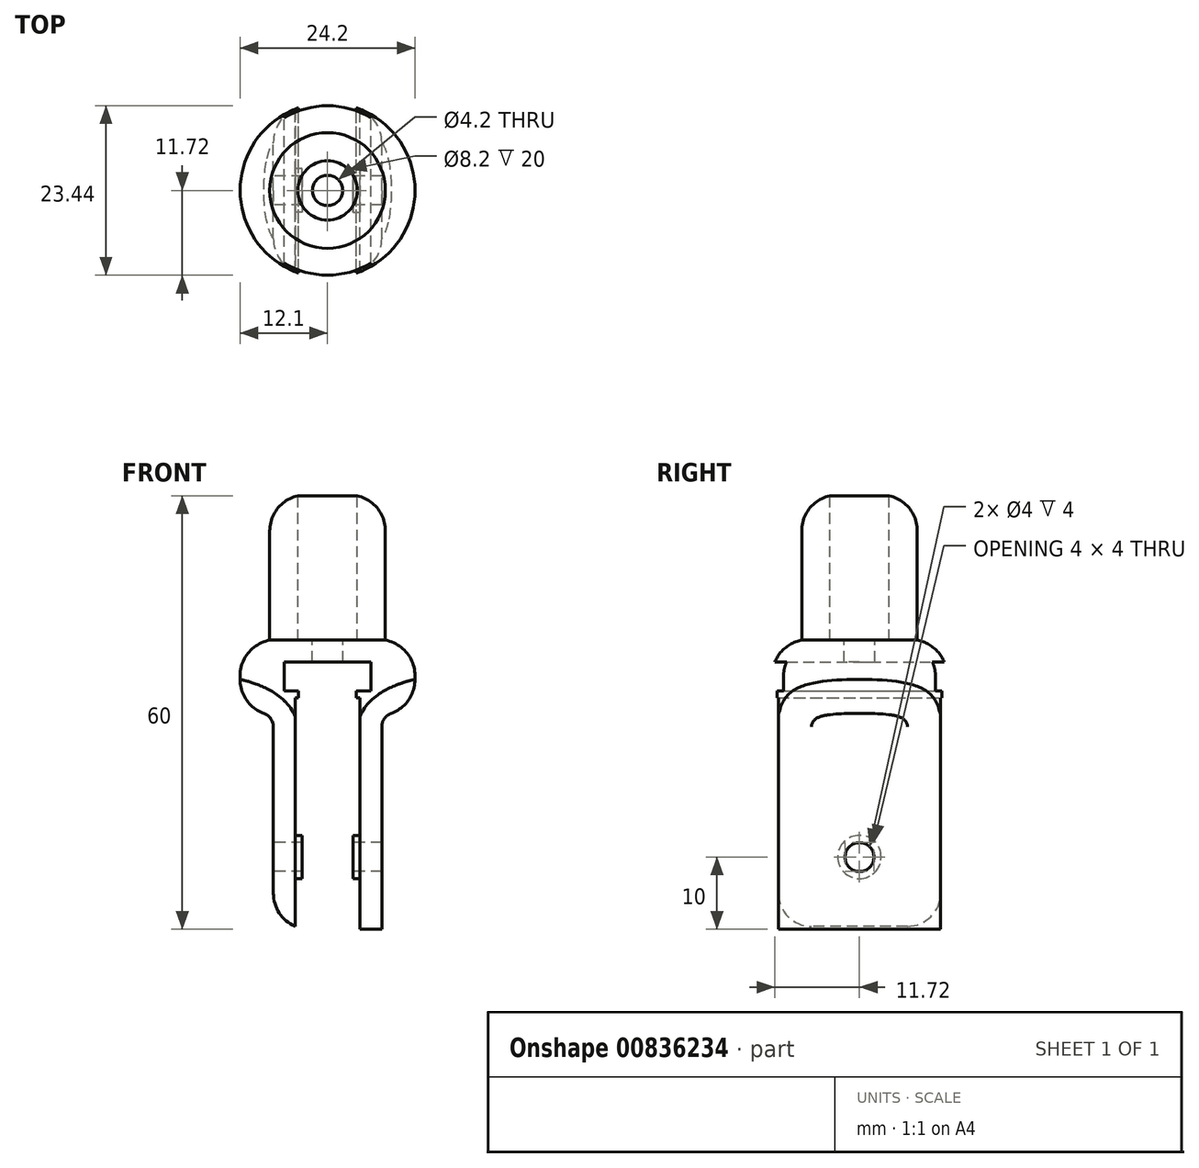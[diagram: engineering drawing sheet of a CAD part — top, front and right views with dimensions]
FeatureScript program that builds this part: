
annotation { "Feature Type Name" : "Feature", "Feature Type Description" : "" }
export const myFeature = defineFeature(function(context is Context, id is Id, definition is map)
    precondition{}
    {
        {
            var Q0;
            Q0=qCreatedBy(makeId("Front.planeOp"),FACE);
            var sketch = newSketch(context, id + "F0", { "sketchPlane" : qUnion([Q0])});
            skLineSegment(sketch, "E0.bottom", {"start": v(-8, 20) * mm, "end": v(-4.1, 20) * mm});
            skLineSegment(sketch, "E0.top", {"start": v(-8, 0) * mm, "end": v(-4.1, 0) * mm});
            skLineSegment(sketch, "E0.left", {"start": v(-8, 20) * mm, "end": v(-8, 0) * mm});
            skLineSegment(sketch, "E0.right", {"start": v(-4.1, 20) * mm, "end": v(-4.1, 0) * mm});
            skLineSegment(sketch, "E1.bottom", {"start": v(-12.1, 0) * mm, "end": v(-2.1, 0) * mm});
            skLineSegment(sketch, "E1.top", {"start": v(-12.1, -40) * mm, "end": v(-2.1, -40) * mm});
            skLineSegment(sketch, "E1.left", {"start": v(-12.1, 0) * mm, "end": v(-12.1, -40) * mm});
            skLineSegment(sketch, "E1.right", {"start": v(-2.1, 0) * mm, "end": v(-2.1, -40) * mm});
            skLineSegment(sketch, "E2", {"start": v(0, 18.35) * mm, "end": v(0, -37.68) * mm, "construction": true});
            skSolve(sketch);
        }
        {
            var Q0;
            Q0 = qSketchRegion(id + "F0", true);
            var Q1;
            Q1=sQuery(id+"F0.wireOp",EDGE,"E2");
            revolve(context, id + "F1", {"surfaceOperationType" : NewSurfaceOperationType.NEW, "entities" : qUnion([Q0]), "axis" : qUnion([Q1]), "revolveType" : RevolveType.FULL});
        }
        {
            var Q0;
            Q0=qCreatedBy(makeId("Front.planeOp"),FACE);
            var sketch = newSketch(context, id + "F2", { "sketchPlane" : qUnion([Q0])});
            skLineSegment(sketch, "E3.bottom", {"start": v(4.5, -40) * mm, "end": v(-4.5, -40) * mm});
            skLineSegment(sketch, "E3.top", {"start": v(4.5, -8) * mm, "end": v(-4.5, -8) * mm});
            skLineSegment(sketch, "E3.left", {"start": v(4.5, -40) * mm, "end": v(4.5, -8) * mm});
            skLineSegment(sketch, "E3.right", {"start": v(-4.5, -40) * mm, "end": v(-4.5, -8) * mm});
            skLineSegment(sketch, "E4.bottom", {"start": v(4, -7) * mm, "end": v(-4, -7) * mm});
            skLineSegment(sketch, "E4.top", {"start": v(4, -8) * mm, "end": v(-4, -8) * mm});
            skLineSegment(sketch, "E4.left", {"start": v(4, -7) * mm, "end": v(4, -8) * mm});
            skLineSegment(sketch, "E4.right", {"start": v(-4, -7) * mm, "end": v(-4, -8) * mm});
            skLineSegment(sketch, "E5.bottom", {"start": v(6, -3) * mm, "end": v(-6, -3) * mm});
            skLineSegment(sketch, "E5.top", {"start": v(6, -7) * mm, "end": v(-6, -7) * mm});
            skLineSegment(sketch, "E5.left", {"start": v(6, -3) * mm, "end": v(6, -7) * mm});
            skLineSegment(sketch, "E5.right", {"start": v(-6, -3) * mm, "end": v(-6, -7) * mm});
            skLineSegment(sketch, "E6.bottom", {"start": v(-9.5, -10) * mm, "end": v(-12.1, -10) * mm});
            skLineSegment(sketch, "E6.top", {"start": v(-7.5, -40) * mm, "end": v(-12.1, -40) * mm});
            skLineSegment(sketch, "E6.left", {"start": v(-7.5, -12) * mm, "end": v(-7.5, -40) * mm});
            skLineSegment(sketch, "E6.right", {"start": v(-12.1, -10) * mm, "end": v(-12.1, -40) * mm});
            skPoint(sketch, "E7.visualSharp", {"position": v(-7.5, -10) * mm});
            skArc(sketch, "E7.filletArc", {"start": v(-7.5, -12) * mm, "mid": v(-8.09, -10.59) * mm, "end": v(-9.5, -10) * mm});
            skLineSegment(sketch, "E8.MirrorCS", {"start": v(7.5, -12) * mm, "end": v(7.5, -40) * mm});
            skArc(sketch, "E9.MirrorCS", {"start": v(7.5, -12) * mm, "mid": v(8.09, -10.59) * mm, "end": v(9.5, -10) * mm});
            skLineSegment(sketch, "E10.MirrorCS", {"start": v(9.5, -10) * mm, "end": v(12.1, -10) * mm});
            skLineSegment(sketch, "E11.MirrorCS", {"start": v(12.1, -10) * mm, "end": v(12.1, -40) * mm});
            skLineSegment(sketch, "E12.MirrorCS", {"start": v(7.5, -40) * mm, "end": v(12.1, -40) * mm});
            skSolve(sketch);
        }
        {
            var Q0;
            Q0 = qSketchRegion(id + "F2", true);
            extrude(context, id + "F3", {"entities" : qUnion([Q0]), "operationType" : NewBodyOperationType.REMOVE, "endBound" : BoundingType.SYMMETRIC, "depth" : 50 * mm, "offsetDistance" : 25 * mm});
        }
        {
            var Q0;
            Q0=makeQuery(id+"F3.boolean.opBoolean","COPY",FACE,{"derivedFrom":makeQuery(id+"F3.opExtrude","SWEPT_FACE",FACE,{"disambiguationData":[OSD([sQuery(id+"F2.wireOp",EDGE,"E3.left")])]})});
            var sketch = newSketch(context, id + "F4", { "sketchPlane" : qUnion([Q0])});
            skCircle(sketch, "E13", {"center": v(0, -30) * mm, "radius": 2 * mm});
            skSolve(sketch);
        }
        {
            var Q0;
            Q0 = qSketchRegion(id + "F4", true);
            extrude(context, id + "F5", {"entities" : qUnion([Q0]), "operationType" : NewBodyOperationType.REMOVE, "endBound" : BoundingType.SYMMETRIC, "oppositeDirection" : true, "depth" : 50 * mm, "offsetDistance" : 25 * mm});
        }
        {
            var Q0;
            Q0=makeQuery(id+"F3.boolean.opBoolean","COPY",FACE,{"derivedFrom":makeQuery(id+"F3.opExtrude","SWEPT_FACE",FACE,{"disambiguationData":[OSD([sQuery(id+"F2.wireOp",EDGE,"E3.right")])]})});
            var sketch = newSketch(context, id + "F6", { "sketchPlane" : qUnion([Q0])});
            skCircle(sketch, "E14", {"center": v(0, -30) * mm, "radius": 3 * mm});
            skSolve(sketch);
        }
        {
            var Q0;
            Q0=makeQuery(id+"F6.imprint","IMPRINT",FACE,{"disambiguationData":[TD([[makeQuery(id+"F6.imprint","IMPRINT",EDGE,{"derivedFrom":sQuery(id+"F6.wireOp",EDGE,"E14")}),1.0]])]});
            extrude(context, id + "F7", {"entities" : qUnion([Q0]), "operationType" : NewBodyOperationType.ADD, "depth" : 1 * mm, "offsetDistance" : 25 * mm});
        }
        {
            var Q0;
            Q0=makeQuery(id+"F3.boolean.opBoolean","COPY",FACE,{"derivedFrom":makeQuery(id+"F3.opExtrude","SWEPT_FACE",FACE,{"disambiguationData":[OSD([sQuery(id+"F2.wireOp",EDGE,"E3.left")])]})});
            var sketch = newSketch(context, id + "F8", { "sketchPlane" : qUnion([Q0])});
            skCircle(sketch, "E15", {"center": v(0, -30) * mm, "radius": 3 * mm});
            skSolve(sketch);
        }
        {
            var Q0;
            Q0=makeQuery(id+"F8.imprint","IMPRINT",FACE,{"disambiguationData":[TD([[makeQuery(id+"F8.imprint","IMPRINT",EDGE,{"derivedFrom":sQuery(id+"F8.wireOp",EDGE,"E15")}),1.0]])]});
            extrude(context, id + "F9", {"entities" : qUnion([Q0]), "operationType" : NewBodyOperationType.ADD, "depth" : 1 * mm, "offsetDistance" : 25 * mm});
        }
        {
            var Q0;
            {var subQ0=sQuery(id+"F0.wireOp",EDGE,"E1.top");var subQ1=sQuery(id+"F0.wireOp",EDGE,"E1.left");Q0=makeQuery(id+"F3.boolean.opBoolean","SPLIT",EDGE,{"disambiguationData":[TD([makeQuery(id+"F1.opRevolve","SWEPT_FACE",FACE,{"disambiguationData":[OSD([subQ0])]}),makeQuery(id+"F1.opRevolve","SWEPT_FACE",FACE,{"disambiguationData":[OSD([subQ1])]}),makeQuery(id+"F3.opExtrude","SWEPT_FACE",FACE,{"disambiguationData":[OSD([sQuery(id+"F2.wireOp",EDGE,"E3.right")])]}),makeQuery(id+"F3.opExtrude","SWEPT_FACE",FACE,{"disambiguationData":[OSD([sQuery(id+"F2.wireOp",EDGE,"E6.left")])]})]),OD(1.0)],"derivedFrom":makeQuery(id+"F1.opRevolve","SWEPT_EDGE",EDGE,{"disambiguationData":[OSD([subQ0,subQ1])]})});}
            var Q1;
            {var subQ0=sQuery(id+"F0.wireOp",EDGE,"E1.top");var subQ1=sQuery(id+"F0.wireOp",EDGE,"E1.left");Q1=makeQuery(id+"F3.boolean.opBoolean","SPLIT",EDGE,{"disambiguationData":[TD([makeQuery(id+"F1.opRevolve","SWEPT_FACE",FACE,{"disambiguationData":[OSD([subQ0])]}),makeQuery(id+"F1.opRevolve","SWEPT_FACE",FACE,{"disambiguationData":[OSD([subQ1])]}),makeQuery(id+"F3.opExtrude","SWEPT_FACE",FACE,{"disambiguationData":[OSD([sQuery(id+"F2.wireOp",EDGE,"E3.left")])]}),makeQuery(id+"F3.opExtrude","SWEPT_FACE",FACE,{"disambiguationData":[OSD([sQuery(id+"F2.wireOp",EDGE,"E8.MirrorCS")])]})]),OD(1.0)],"derivedFrom":makeQuery(id+"F1.opRevolve","SWEPT_EDGE",EDGE,{"disambiguationData":[OSD([subQ0,subQ1])]})});}
            var Q2;
            {var subQ0=sQuery(id+"F0.wireOp",EDGE,"E1.top");var subQ1=sQuery(id+"F0.wireOp",EDGE,"E1.left");Q2=makeQuery(id+"F3.boolean.opBoolean","SPLIT",EDGE,{"disambiguationData":[TD([makeQuery(id+"F1.opRevolve","SWEPT_FACE",FACE,{"disambiguationData":[OSD([subQ0])]}),makeQuery(id+"F1.opRevolve","SWEPT_FACE",FACE,{"disambiguationData":[OSD([subQ1])]}),makeQuery(id+"F3.opExtrude","SWEPT_FACE",FACE,{"disambiguationData":[OSD([sQuery(id+"F2.wireOp",EDGE,"E3.right")])]}),makeQuery(id+"F3.opExtrude","SWEPT_FACE",FACE,{"disambiguationData":[OSD([sQuery(id+"F2.wireOp",EDGE,"E6.left")])]})]),OD(0.0)],"derivedFrom":makeQuery(id+"F1.opRevolve","SWEPT_EDGE",EDGE,{"disambiguationData":[OSD([subQ0,subQ1])]})});}
            var Q3;
            {var subQ0=sQuery(id+"F0.wireOp",EDGE,"E1.top");var subQ1=sQuery(id+"F0.wireOp",EDGE,"E1.left");Q3=makeQuery(id+"F3.boolean.opBoolean","SPLIT",EDGE,{"disambiguationData":[TD([makeQuery(id+"F1.opRevolve","SWEPT_FACE",FACE,{"disambiguationData":[OSD([subQ0])]}),makeQuery(id+"F1.opRevolve","SWEPT_FACE",FACE,{"disambiguationData":[OSD([subQ1])]}),makeQuery(id+"F3.opExtrude","SWEPT_FACE",FACE,{"disambiguationData":[OSD([sQuery(id+"F2.wireOp",EDGE,"E3.left")])]}),makeQuery(id+"F3.opExtrude","SWEPT_FACE",FACE,{"disambiguationData":[OSD([sQuery(id+"F2.wireOp",EDGE,"E8.MirrorCS")])]})]),OD(0.0)],"derivedFrom":makeQuery(id+"F1.opRevolve","SWEPT_EDGE",EDGE,{"disambiguationData":[OSD([subQ0,subQ1])]})});}
            var Q4;
            Q4=makeQuery(id+"F1.opRevolve","SWEPT_EDGE",EDGE,{"disambiguationData":[OSD([sQuery(id+"F0.wireOp",EDGE,"E1.bottom"),sQuery(id+"F0.wireOp",EDGE,"E1.left")])]});
            var Q5;
            Q5=makeQuery(id+"F1.opRevolve","SWEPT_EDGE",EDGE,{"disambiguationData":[OSD([sQuery(id+"F0.wireOp",EDGE,"E0.bottom"),sQuery(id+"F0.wireOp",EDGE,"E0.left")])]});
            var Q6;
            Q6=makeQuery(id+"F3.boolean.opBoolean","INTERSECT",EDGE,{"derivedFrom":[makeQuery(id+"F1.opRevolve","SWEPT_FACE",FACE,{"disambiguationData":[OSD([sQuery(id+"F0.wireOp",EDGE,"E1.left")])]}),makeQuery(id+"F3.opExtrude","SWEPT_FACE",FACE,{"disambiguationData":[OSD([sQuery(id+"F2.wireOp",EDGE,"E10.MirrorCS")])]})]});
            var Q7;
            Q7=makeQuery(id+"F3.boolean.opBoolean","INTERSECT",EDGE,{"derivedFrom":[makeQuery(id+"F1.opRevolve","SWEPT_FACE",FACE,{"disambiguationData":[OSD([sQuery(id+"F0.wireOp",EDGE,"E1.left")])]}),makeQuery(id+"F3.opExtrude","SWEPT_FACE",FACE,{"disambiguationData":[OSD([sQuery(id+"F2.wireOp",EDGE,"E6.bottom")])]})]});
            fillet(context, id + "F10", {"entities" : qUnion([Q0, Q1, Q2, Q3, Q4, Q5, Q6, Q7]), "radius" : 5 * mm, "tangentPropagation" : true, "allowEdgeOverflow" : false});
        }
        {
            var Q0;
            Q0=makeQuery(id+"F3.boolean.opBoolean","COPY",EDGE,{"derivedFrom":makeQuery(id+"F3.opExtrude","SWEPT_EDGE",EDGE,{"disambiguationData":[OSD([sQuery(id+"F2.wireOp",EDGE,"E6.top"),sQuery(id+"F2.wireOp",EDGE,"E6.left")])]})});
            var Q1;
            Q1=makeQuery(id+"F3.boolean.opBoolean","COPY",EDGE,{"derivedFrom":makeQuery(id+"F3.opExtrude","SWEPT_EDGE",EDGE,{"disambiguationData":[OSD([sQuery(id+"F2.wireOp",EDGE,"E8.MirrorCS"),sQuery(id+"F2.wireOp",EDGE,"E12.MirrorCS")])]})});
            fillet(context, id + "F11", {"entities" : qUnion([Q0, Q1]), "radius" : 5 * mm, "tangentPropagation" : true, "allowEdgeOverflow" : false});
        }
    });
